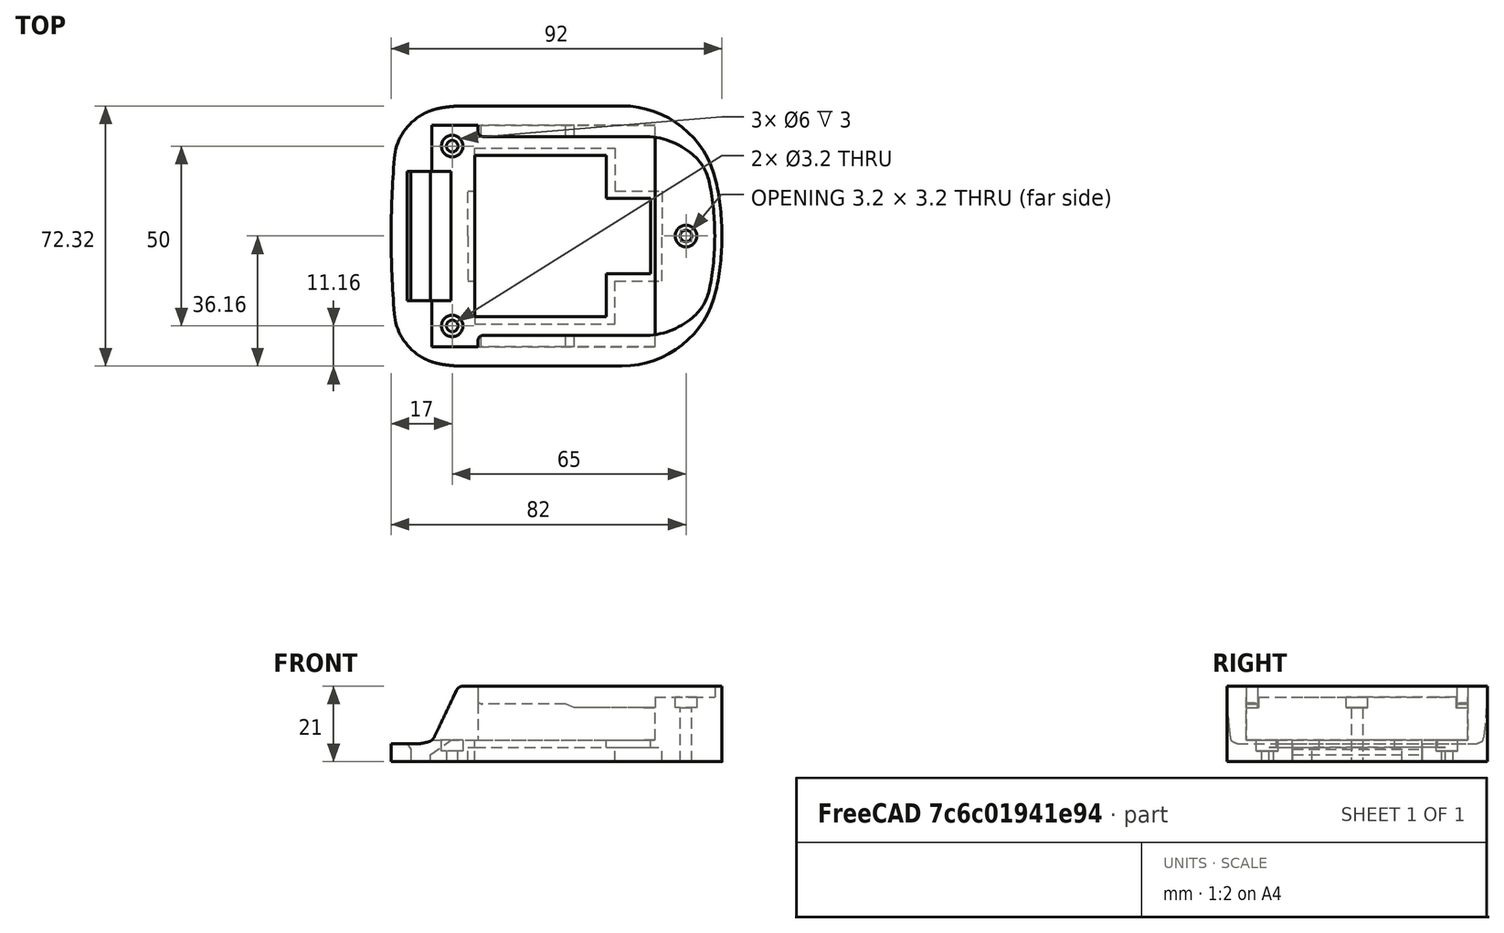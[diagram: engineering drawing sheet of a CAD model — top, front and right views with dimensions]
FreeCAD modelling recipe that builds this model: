
FCSTD DOCUMENT  (FreeCAD 0.21R33771 (Git))
Label: Makita LXT  - 18V - Battery holder
License: Creative Commons Attribution 4.0
LicenseURL: https://creativecommons.org/licenses/by/4.0/
objects: Sketcher::SketchObject×9, PartDesign::Pocket×8, Mesh::Feature×1, PartDesign::Pad×1, Part::Feature×1, PartDesign::Body×1
note: 29 computed .brp shape members not serialized (recipe doc carries the construction recipe); baked Part::Feature solids carry a one-line shape summary decoded from their .brp

FEATURE [Sketcher::SketchObject] Sketch
  FullyConstrained = false
  MapMode = 5
  Support = -> [XY_Plane]
  sketch-geometry (26):
    g0: ArcOfCircle CenterX=259.65 CenterY=-2.5774e-06 CenterZ=0 NormalX=0 NormalY=0 NormalZ=1 AngleXU=0 Radius=259.65 StartAngle=3.05831 EndAngle=3.14159
    g1: ArcOfCircle CenterX=16.3351 CenterY=20.3115 CenterZ=0 NormalX=0 NormalY=0 NormalZ=1 AngleXU=0 Radius=15.4888 StartAngle=1.76803 EndAngle=3.05831
    g2: LineSegment StartX=20 StartY=36.1629 StartZ=0 EndX=64.2 EndY=36.1629 EndZ=0
    g3: ArcOfCircle CenterX=64.2 CenterY=9.3939 CenterZ=0 NormalX=0 NormalY=0 NormalZ=1 AngleXU=0 Radius=26.769 StartAngle=0.218634 EndAngle=1.5708
    g4: ArcOfCircle CenterX=21.9206 CenterY=0 CenterZ=0 NormalX=0 NormalY=0 NormalZ=1 AngleXU=0 Radius=70.0794 StartAngle=0 EndAngle=0.218634
    g5: ArcOfCircle CenterX=20 CenterY=1.97116 CenterZ=0 NormalX=0 NormalY=0 NormalZ=1 AngleXU=0 Radius=34.1917 StartAngle=1.5708 EndAngle=1.76803
    g6: Circle CenterX=17 CenterY=25 CenterZ=0 NormalX=0 NormalY=0 NormalZ=1 AngleXU=0 Radius=1.6
    g7: ArcOfCircle CenterX=82 CenterY=0 CenterZ=0 NormalX=0 NormalY=0 NormalZ=1 AngleXU=0 Radius=1.6 StartAngle=0 EndAngle=3.14159
    g8: LineSegment StartX=23.3 StartY=0 StartZ=0 EndX=23.3 EndY=22.4 EndZ=0
    g9: LineSegment StartX=23.3 StartY=22.4 StartZ=0 EndX=59.9 EndY=22.4 EndZ=0
    g10: LineSegment StartX=59.9 StartY=22.4 StartZ=0 EndX=59.9 EndY=10.5 EndZ=0
    g11: LineSegment StartX=59.9 StartY=10.5 StartZ=0 EndX=72.1 EndY=10.5 EndZ=0
    g12: LineSegment StartX=72.1 StartY=10.5 StartZ=0 EndX=72.1 EndY=0 EndZ=0
    g13: ArcOfCircle CenterX=259.65 CenterY=2.5774e-06 CenterZ=0 NormalX=0 NormalY=0 NormalZ=1 AngleXU=0 Radius=259.65 StartAngle=3.14159 EndAngle=3.22488
    g14: ArcOfCircle CenterX=16.3351 CenterY=-20.3115 CenterZ=0 NormalX=0 NormalY=0 NormalZ=1 AngleXU=0 Radius=15.4888 StartAngle=3.22488 EndAngle=4.51516
    g15: LineSegment StartX=20 StartY=-36.1629 StartZ=0 EndX=64.2 EndY=-36.1629 EndZ=0
    g16: ArcOfCircle CenterX=64.2 CenterY=-9.3939 CenterZ=0 NormalX=0 NormalY=0 NormalZ=1 AngleXU=0 Radius=26.769 StartAngle=4.71239 EndAngle=6.06455
    g17: ArcOfCircle CenterX=21.9206 CenterY=0 CenterZ=0 NormalX=0 NormalY=0 NormalZ=1 AngleXU=0 Radius=70.0794 StartAngle=6.06455 EndAngle=6.28319
    g18: ArcOfCircle CenterX=20 CenterY=-1.97116 CenterZ=0 NormalX=0 NormalY=0 NormalZ=1 AngleXU=0 Radius=34.1917 StartAngle=4.51516 EndAngle=4.71239
    g19: Circle CenterX=17 CenterY=-25 CenterZ=0 NormalX=0 NormalY=0 NormalZ=1 AngleXU=0 Radius=1.6
    g20: ArcOfCircle CenterX=82 CenterY=0 CenterZ=0 NormalX=0 NormalY=0 NormalZ=1 AngleXU=0 Radius=1.6 StartAngle=3.14159 EndAngle=6.28319
    g21: LineSegment StartX=23.3 StartY=0 StartZ=0 EndX=23.3 EndY=-22.4 EndZ=0
    g22: LineSegment StartX=23.3 StartY=-22.4 StartZ=0 EndX=59.9 EndY=-22.4 EndZ=0
    g23: LineSegment StartX=59.9 StartY=-22.4 StartZ=0 EndX=59.9 EndY=-10.5 EndZ=0
    g24: LineSegment StartX=59.9 StartY=-10.5 StartZ=0 EndX=72.1 EndY=-10.5 EndZ=0
    g25: LineSegment StartX=72.1 StartY=-10.5 StartZ=0 EndX=72.1 EndY=0 EndZ=0
  constraints (59):
    c: Horizontal(g2)
    c: DistanceX(g2) = 20
    c: DistanceX(g2,g2) = 44.2
    c: Tangent(g4,g3) = -1.5708
    c: Tangent(g3,g2) = 1.5708
    c: Tangent(g1,g0) = -1.5708
    c: Tangent(g5,g2) = 1.5708
    c: Tangent(g5,g1) = -1.5708
    c: DistanceX(g0) = 0.9
    c: DistanceX(g1) = 13.3
    c: DistanceX(g4) = 92
    c: Coincident(g0,g-1)
    c: DistanceY(g0) = 21.6
    c: DistanceY(g1) = 35.5
    c: PointOnObject(g4,g-1)
    c: DistanceY(g3) = 15.2
    c: DistanceY(g6) = 25
    c: DistanceX(g6) = 17
    c: Diameter(g6) = 3.2
    c: PointOnObject(g7,g-1)
    c: PointOnObject(g7,g-1)
    c: PointOnObject(g7,g-1)
    c: DistanceX(g6,g7) = 65
    c: Equal(g7,g6)
    c: Tangent(g0,g-2)
    c: Perpendicular(g4,g-1)
    c: PointOnObject(g8,g-1)
    c: Vertical(g8)
    c: Coincident(g8,g9)
    c: Horizontal(g9)
    c: Coincident(g9,g10)
    c: Vertical(g10)
    c: Coincident(g10,g11)
    c: Horizontal(g11)
    c: Coincident(g11,g12)
    c: Vertical(g12)
    c: DistanceX(g8) = 23.3
    c: DistanceY(g8) = 22.4
    c: DistanceX(g9,g9) = 36.6
    c: DistanceY(g10,g10) = 11.9
    c: DistanceX(g11,g11) = 12.2
    c: PointOnObject(g12,g-1)
    c: Horizontal(g15)
    c: Tangent(g17,g16) = -1.5708
    c: Tangent(g16,g15) = -1.5708
    c: Tangent(g14,g13) = -1.5708
    c: Tangent(g18,g15) = -1.5708
    c: Tangent(g18,g14) = -1.5708
    c: Diameter(g19) = 3.2
    c: Equal(g20,g19)
    c: Vertical(g21)
    c: Coincident(g21,g22)
    c: Horizontal(g22)
    c: Coincident(g22,g23)
    c: Vertical(g23)
    c: Coincident(g23,g24)
    c: Horizontal(g24)
    c: Coincident(g24,g25)
    c: Vertical(g25)
FEATURE [Mesh::Feature] Makita_18V_Body  label="Makita 18V-Body"
  Placement = pos=(17,0,0) rot=(0,0,1;0rad)
FEATURE [PartDesign::Pad] Pad
  Direction = (0,0,1)
  Length = 21
  Length2 = 10
  Profile = -> Sketch
  ReferenceAxis = -> Sketch [N_Axis]
  Type = 0
FEATURE [Sketcher::SketchObject] Sketch001
  FullyConstrained = true
  MapMode = 5
  Placement = pos=(0,0,0) rot=(1,0,0;1.5708rad)
  Support = -> [XZ_Plane]
  sketch-geometry (8):
    g0: LineSegment StartX=0 StartY=5 StartZ=0 EndX=0 EndY=21 EndZ=0
    g1: LineSegment StartX=0 StartY=21 StartZ=0 EndX=20 EndY=21 EndZ=0
    g2: LineSegment StartX=0 StartY=5 StartZ=0 EndX=7.9 EndY=5 EndZ=0
    g3: LineSegment StartX=18.2 StartY=19.8659 StartZ=0 EndX=11.9 EndY=6.7 EndZ=0
    g4: ArcOfCircle CenterX=20 CenterY=19.0045 CenterZ=0 NormalX=0 NormalY=0 NormalZ=1 AngleXU=0 Radius=1.99546 StartAngle=1.5708 EndAngle=2.69528
    g5: ArcOfCircle CenterX=10.0257 CenterY=7.59685 CenterZ=0 NormalX=0 NormalY=0 NormalZ=1 AngleXU=0 Radius=2.07779 StartAngle=4.99242 EndAngle=5.83688
    g6: ArcOfCircle CenterX=7.9 CenterY=5.60003 CenterZ=0 NormalX=0 NormalY=0 NormalZ=1 AngleXU=0 Radius=0.600034 StartAngle=4.71239 EndAngle=4.87983
    g7: ArcOfCircle CenterX=4.0509 CenterY=28.3729 CenterZ=0 NormalX=0 NormalY=0 NormalZ=1 AngleXU=0 Radius=23.6959 StartAngle=4.87983 EndAngle=4.99242
  constraints (22):
    c: PointOnObject(g0,g-2)
    c: PointOnObject(g0,g-2)
    c: Horizontal(g1)
    c: Coincident(g1,g0)
    c: DistanceY(g0) = 5
    c: DistanceY(g0) = 21
    c: Coincident(g2,g0)
    c: Horizontal(g2)
    c: Tangent(g4,g3) = -1.5708
    c: Tangent(g5,g3) = 1.5708
    c: Tangent(g4,g1) = 1.5708
    c: DistanceX(g1,g1) = 20
    c: DistanceX(g3) = 11.9
    c: DistanceY(g3) = 6.7
    c: DistanceX(g3) = 18.2
    c: Tangent(g6,g2) = -1.5708
    c: DistanceX(g2,g2) = 7.9
    c: Tangent(g7,g5) = -1.5708
    c: Tangent(g7,g6) = -1.5708
    c: DistanceX(g2,g6) = 0.1
    c: DistanceX(g5) = 10.6
    c: DistanceY(g5) = 5.6
FEATURE [PartDesign::Pocket] Pocket
  BaseFeature = -> Pad
  Direction = (0,1,-2e-16)
  Length = 5
  Length2 = 5
  Midplane = true
  Profile = -> Sketch001
  ReferenceAxis = -> Sketch001 [N_Axis]
  Type = 1
FEATURE [Part::Feature] Makita_18V_Body001
  shape: bbox 92 x 71 x 21 mm, 5406 faces, 0 solids (baked)
FEATURE [Sketcher::SketchObject] Sketch002
  FullyConstrained = false
  MapMode = 5
  Placement = pos=(0,0,21) rot=(0,0,1;0rad)
  Support = -> [Pocket]
  sketch-geometry (16):
    g0: LineSegment StartX=24.2 StartY=30.78 StartZ=0 EndX=0 EndY=30.78 EndZ=0
    g1: LineSegment StartX=24.2 StartY=30.78 StartZ=0 EndX=24.2 EndY=28.88 EndZ=0
    g2: LineSegment StartX=25.4 StartY=27.68 StartZ=0 EndX=70.2 EndY=27.68 EndZ=0
    g3: ArcOfCircle CenterX=25.4 CenterY=28.88 CenterZ=0 NormalX=0 NormalY=0 NormalZ=1 AngleXU=0 Radius=1.2 StartAngle=3.14159 EndAngle=4.71239
    g4: ArcOfCircle CenterX=15.7361 CenterY=0 CenterZ=0 NormalX=0 NormalY=0 NormalZ=1 AngleXU=0 Radius=74.2639 StartAngle=0 EndAngle=0.199259
    g5: ArcOfCircle CenterX=74.666 CenterY=11.9002 CenterZ=0 NormalX=0 NormalY=0 NormalZ=1 AngleXU=0 Radius=14.1444 StartAngle=0.199259 EndAngle=0.868771
    g6: ArcOfCircle CenterX=70.2 CenterY=6.61972 CenterZ=0 NormalX=0 NormalY=0 NormalZ=1 AngleXU=0 Radius=21.0603 StartAngle=0.868771 EndAngle=1.5708
    g7: LineSegment StartX=0 StartY=0 StartZ=0 EndX=0 EndY=30.78 EndZ=0
    g8: LineSegment StartX=24.2 StartY=-30.78 StartZ=0 EndX=0 EndY=-30.78 EndZ=0
    g9: LineSegment StartX=24.2 StartY=-30.78 StartZ=0 EndX=24.2 EndY=-28.88 EndZ=0
    g10: LineSegment StartX=25.4 StartY=-27.68 StartZ=0 EndX=70.2 EndY=-27.68 EndZ=0
    g11: ArcOfCircle CenterX=25.4 CenterY=-28.88 CenterZ=0 NormalX=0 NormalY=0 NormalZ=1 AngleXU=0 Radius=1.2 StartAngle=1.5708 EndAngle=3.14159
    g12: ArcOfCircle CenterX=15.7361 CenterY=0 CenterZ=0 NormalX=0 NormalY=0 NormalZ=1 AngleXU=0 Radius=74.2639 StartAngle=6.08393 EndAngle=6.28319
    g13: ArcOfCircle CenterX=74.666 CenterY=-11.9002 CenterZ=0 NormalX=0 NormalY=0 NormalZ=1 AngleXU=0 Radius=14.1444 StartAngle=5.41441 EndAngle=6.08393
    g14: ArcOfCircle CenterX=70.2 CenterY=-6.61972 CenterZ=0 NormalX=0 NormalY=0 NormalZ=1 AngleXU=0 Radius=21.0603 StartAngle=4.71239 EndAngle=5.41441
    g15: LineSegment StartX=0 StartY=0 StartZ=0 EndX=0 EndY=-30.78 EndZ=0
  constraints (36):
    c: PointOnObject(g0,g-2)
    c: Horizontal(g0)
    c: DistanceY(g0) = 30.78
    c: DistanceX(g0,g0) = 24.2
    c: Coincident(g1,g0)
    c: Vertical(g1)
    c: Horizontal(g2)
    c: Tangent(g3,g1) = -1.5708
    c: Tangent(g3,g2) = -1.5708
    c: DistanceY(g1,g1) = 1.9
    c: Radius(g3) = 1.2
    c: PointOnObject(g4,g-1)
    c: Perpendicular(g4,g-1)
    c: DistanceX(g4) = 90
    c: DistanceY(g4) = 14.7
    c: Tangent(g6,g5) = -1.5708
    c: Tangent(g5,g4) = -1.5708
    c: Tangent(g6,g2) = 1.5708
    c: DistanceX(g2,g2) = 44.8
    c: DistanceX(g5) = 83.8
    c: DistanceY(g5) = 22.7
    c: PointOnObject(g7,g-1)
    c: Coincident(g7,g0)
    c: Vertical(g7)
    c: Horizontal(g8)
    c: Coincident(g9,g8)
    c: Vertical(g9)
    c: Horizontal(g10)
    c: Tangent(g11,g9) = 1.5708
    c: Tangent(g11,g10) = 1.5708
    c: Radius(g11) = 1.2
    c: Tangent(g14,g13) = -1.5708
    c: Tangent(g13,g12) = -1.5708
    c: Tangent(g14,g10) = -1.5708
    c: Coincident(g15,g8)
    c: Vertical(g15)
FEATURE [PartDesign::Pocket] Pocket001
  BaseFeature = -> Pocket
  Direction = (0,0,-1)
  Length = 3
  Length2 = 5
  Profile = -> Sketch002
  ReferenceAxis = -> Sketch002 [N_Axis]
  Type = 0
FEATURE [Sketcher::SketchObject] Sketch003
  ExternalGeometry = -> [Sketch002]
  FullyConstrained = false
  MapMode = 5
  Placement = pos=(0,0,18) rot=(0,0,1;0rad)
  Support = -> [Pocket001]
  sketch-geometry (14):
    g0: LineSegment StartX=0 StartY=0 StartZ=0 EndX=0 EndY=30.78 EndZ=0
    g1: LineSegment StartX=0 StartY=30.78 StartZ=0 EndX=24.2 EndY=30.78 EndZ=0
    g2: LineSegment StartX=24.2 StartY=28.88 StartZ=0 EndX=24.2 EndY=30.78 EndZ=0
    g3: LineSegment StartX=25.4 StartY=27.68 StartZ=0 EndX=70.2 EndY=27.68 EndZ=0
    g4: ArcOfCircle CenterX=25.4 CenterY=28.88 CenterZ=0 NormalX=0 NormalY=0 NormalZ=1 AngleXU=0 Radius=1.2 StartAngle=3.14159 EndAngle=4.71239
    g5: LineSegment StartX=73.4 StartY=27.4355 StartZ=0 EndX=73.4 EndY=0 EndZ=0
    g6: ArcOfCircle CenterX=70.2 CenterY=6.61972 CenterZ=0 NormalX=0 NormalY=0 NormalZ=1 AngleXU=0 Radius=21.0603 StartAngle=1.41826 EndAngle=1.5708
    g7: LineSegment StartX=0 StartY=0 StartZ=0 EndX=0 EndY=-30.78 EndZ=0
    g8: LineSegment StartX=0 StartY=-30.78 StartZ=0 EndX=24.2 EndY=-30.78 EndZ=0
    g9: LineSegment StartX=24.2 StartY=-28.88 StartZ=0 EndX=24.2 EndY=-30.78 EndZ=0
    g10: LineSegment StartX=25.4 StartY=-27.68 StartZ=0 EndX=70.2 EndY=-27.68 EndZ=0
    g11: ArcOfCircle CenterX=25.4 CenterY=-28.88 CenterZ=0 NormalX=0 NormalY=0 NormalZ=1 AngleXU=0 Radius=1.2 StartAngle=1.5708 EndAngle=3.14159
    g12: LineSegment StartX=73.4 StartY=-27.4355 StartZ=0 EndX=73.4 EndY=0 EndZ=0
    g13: ArcOfCircle CenterX=70.2 CenterY=-6.61972 CenterZ=0 NormalX=0 NormalY=0 NormalZ=1 AngleXU=0 Radius=21.0603 StartAngle=4.71239 EndAngle=4.86492
  constraints (23):
    c: Coincident(g0,g-3)
    c: Coincident(g0,g-4)
    c: Coincident(g1,g0)
    c: Coincident(g1,g-4)
    c: Coincident(g2,g-7)
    c: Coincident(g2,g1)
    c: Coincident(g3,g-5)
    c: Coincident(g3,g-6)
    c: Coincident(g4,g2)
    c: Tangent(g4,g3) = -1.5708
    c: PointOnObject(g5,g-6)
    c: PointOnObject(g5,g-1)
    c: Vertical(g5)
    c: Coincident(g6,g5)
    c: Tangent(g6,g3) = 1.5708
    c: DistanceX(g5) = 73.4
    c: Coincident(g8,g7)
    c: Coincident(g9,g8)
    c: Coincident(g11,g9)
    c: Tangent(g11,g10) = 1.5708
    c: Vertical(g12)
    c: Coincident(g13,g12)
    c: Tangent(g13,g10) = -1.5708
FEATURE [PartDesign::Pocket] Pocket002
  BaseFeature = -> Pocket001
  Direction = (0,0,-1)
  Length = 12
  Length2 = 5
  Profile = -> Sketch003
  ReferenceAxis = -> Sketch003 [N_Axis]
  Type = 0
FEATURE [Sketcher::SketchObject] Sketch004
  ExternalGeometry = -> [Pocket002]
  FullyConstrained = true
  MapMode = 5
  Placement = pos=(0,0,6) rot=(0,0,1;0rad)
  Support = -> [Pocket002]
  sketch-geometry (2):
    g0: Circle CenterX=17 CenterY=25 CenterZ=0 NormalX=0 NormalY=0 NormalZ=1 AngleXU=0 Radius=3
    g1: Circle CenterX=17 CenterY=-25 CenterZ=0 NormalX=0 NormalY=0 NormalZ=1 AngleXU=0 Radius=3
  constraints (4):
    c: Symmetric(g1,g0,g-1)
    c: Equal(g0,g1)
    c: Coincident(g-3,g0)
    c: Diameter(g0) = 6
FEATURE [PartDesign::Pocket] Pocket003
  BaseFeature = -> Pocket002
  Direction = (0,0,-1)
  Length = 3
  Length2 = 5
  Profile = -> Sketch004
  ReferenceAxis = -> Sketch004 [N_Axis]
  Type = 0
FEATURE [Sketcher::SketchObject] Sketch005
  ExternalGeometry = -> [Pocket003]
  FullyConstrained = true
  MapMode = 5
  Placement = pos=(0,0,18) rot=(0,0,1;0rad)
  Support = -> [Pocket003]
  sketch-geometry (1):
    g0: Circle CenterX=82 CenterY=0 CenterZ=0 NormalX=0 NormalY=0 NormalZ=1 AngleXU=0 Radius=3
  constraints (2):
    c: Coincident(g0,g-3)
    c: Diameter(g0) = 6
FEATURE [PartDesign::Pocket] Pocket004
  BaseFeature = -> Pocket003
  Direction = (0,0,-1)
  Length = 3
  Length2 = 5
  Profile = -> Sketch005
  ReferenceAxis = -> Sketch005 [N_Axis]
  Type = 0
FEATURE [Sketcher::SketchObject] Sketch006
  ExternalGeometry = -> [Sketch003]
  FullyConstrained = true
  MapMode = 5
  Placement = pos=(0,0,0) rot=(1,0,0;1.5708rad)
  Support = -> [XZ_Plane]
  sketch-geometry (7):
    g0: LineSegment StartX=73.4 StartY=15 StartZ=0 EndX=51 EndY=15 EndZ=0
    g1: LineSegment StartX=51 StartY=15 StartZ=0 EndX=48.5 EndY=16 EndZ=0
    g2: LineSegment StartX=48.5 StartY=16 StartZ=0 EndX=25 EndY=16 EndZ=0
    g3: LineSegment StartX=24.2 StartY=16.4 StartZ=0 EndX=25 EndY=16 EndZ=0
    g4: LineSegment StartX=24.2 StartY=16.4 StartZ=0 EndX=24.2 EndY=6 EndZ=0
    g5: LineSegment StartX=24.2 StartY=6 StartZ=0 EndX=73.4 EndY=6 EndZ=0
    g6: LineSegment StartX=73.4 StartY=6 StartZ=0 EndX=73.4 EndY=15 EndZ=0
  constraints (21):
    c: Horizontal(g0)
    c: Coincident(g1,g0)
    c: Coincident(g2,g1)
    c: Horizontal(g2)
    c: Coincident(g2,g3)
    c: Coincident(g4,g3)
    c: Vertical(g4)
    c: Coincident(g5,g4)
    c: Horizontal(g5)
    c: Coincident(g6,g5)
    c: Coincident(g6,g0)
    c: Vertical(g6)
    c: Vertical(g0,g-3)
    c: Vertical(g3,g-5)
    c: DistanceY(g4) = 6
    c: DistanceY(g4,g4) = 10.4
    c: DistanceY(g2) = 16
    c: DistanceX(g3,g2) = 0.8
    c: DistanceX(g2,g2) = 23.5
    c: DistanceY(g0) = 15
    c: DistanceX(g1,g0) = 2.5
FEATURE [PartDesign::Pocket] Pocket005
  BaseFeature = -> Pocket004
  Direction = (0,1,-2e-16)
  Length = 61.6
  Length2 = 5
  Midplane = true
  Profile = -> Sketch006
  ReferenceAxis = -> Sketch006 [N_Axis]
  Type = 0
FEATURE [Sketcher::SketchObject] Sketch007
  ExternalGeometry = -> [Pocket005]
  FullyConstrained = false
  MapMode = 5
  Placement = pos=(0,0,0) rot=(1,0,0;3.14159rad)
  Support = -> [Pocket005]
  sketch-geometry (14):
    g0: LineSegment StartX=21.3 StartY=0 StartZ=0 EndX=21.3 EndY=12.5 EndZ=0
    g1: LineSegment StartX=21.3 StartY=12.5 StartZ=0 EndX=23.3 EndY=12.5 EndZ=0
    g2: LineSegment StartX=23.3 StartY=12.5 StartZ=0 EndX=23.3 EndY=24.5 EndZ=0
    g3: LineSegment StartX=23.3 StartY=24.5 StartZ=0 EndX=62.3 EndY=24.5 EndZ=0
    g4: LineSegment StartX=62.3 StartY=24.5 StartZ=0 EndX=62.3 EndY=12.5 EndZ=0
    g5: LineSegment StartX=62.3 StartY=12.5 StartZ=0 EndX=75.3 EndY=12.5 EndZ=0
    g6: LineSegment StartX=75.3 StartY=12.5 StartZ=0 EndX=75.3 EndY=0 EndZ=0
    g7: LineSegment StartX=21.3 StartY=0 StartZ=0 EndX=21.3 EndY=-12.5 EndZ=0
    g8: LineSegment StartX=21.3 StartY=-12.5 StartZ=0 EndX=23.3 EndY=-12.5 EndZ=0
    g9: LineSegment StartX=23.3 StartY=-12.5 StartZ=0 EndX=23.3 EndY=-24.5 EndZ=0
    g10: LineSegment StartX=23.3 StartY=-24.5 StartZ=0 EndX=62.3 EndY=-24.5 EndZ=0
    g11: LineSegment StartX=62.3 StartY=-24.5 StartZ=0 EndX=62.3 EndY=-12.5 EndZ=0
    g12: LineSegment StartX=62.3 StartY=-12.5 StartZ=0 EndX=75.3 EndY=-12.5 EndZ=0
    g13: LineSegment StartX=75.3 StartY=-12.5 StartZ=0 EndX=75.3 EndY=0 EndZ=0
  constraints (35):
    c: PointOnObject(g0,g-1)
    c: Vertical(g0)
    c: Coincident(g0,g1)
    c: PointOnObject(g1,g-3)
    c: Horizontal(g1)
    c: Coincident(g1,g2)
    c: Vertical(g2)
    c: Coincident(g2,g3)
    c: Horizontal(g3)
    c: Coincident(g3,g4)
    c: Vertical(g4)
    c: Coincident(g4,g5)
    c: Horizontal(g5)
    c: Coincident(g5,g6)
    c: PointOnObject(g6,g-1)
    c: Vertical(g6)
    c: DistanceY(g2) = 24.5
    c: DistanceY(g0,g0) = 12.5
    c: DistanceX(g1,g1) = 2
    c: DistanceX(g-4,g3) = 2.4
    c: DistanceY(g-5,g4) = 2
    c: DistanceX(g-5,g5) = 3.2
    c: Vertical(g7)
    c: Coincident(g7,g8)
    c: Horizontal(g8)
    c: Coincident(g8,g9)
    c: Vertical(g9)
    c: Coincident(g9,g10)
    c: Horizontal(g10)
    c: Coincident(g10,g11)
    c: Vertical(g11)
    c: Coincident(g11,g12)
    c: Horizontal(g12)
    c: Coincident(g12,g13)
    c: Vertical(g13)
FEATURE [PartDesign::Pocket] Pocket006
  BaseFeature = -> Pocket005
  Direction = (0,0,1)
  Length = 4
  Length2 = 5
  Profile = -> Sketch007
  ReferenceAxis = -> Sketch007 [N_Axis]
  Type = 0
FEATURE [Sketcher::SketchObject] Sketch008
  FullyConstrained = true
  MapMode = 5
  Placement = pos=(0,0,0) rot=(1,0,0;1.5708rad)
  Support = -> [XZ_Plane]
  sketch-geometry (7):
    g0: LineSegment StartX=5.5 StartY=0 StartZ=0 EndX=11 EndY=0 EndZ=0
    g1: LineSegment StartX=11 StartY=0 StartZ=0 EndX=11 EndY=2 EndZ=0
    g2: LineSegment StartX=11 StartY=2 StartZ=0 EndX=16.7 EndY=6 EndZ=0
    g3: LineSegment StartX=16.7 StartY=6 StartZ=0 EndX=4.45 EndY=6 EndZ=0
    g4: LineSegment StartX=4.45 StartY=6 StartZ=0 EndX=4.45 EndY=5 EndZ=0
    g5: LineSegment StartX=4.45 StartY=5 StartZ=0 EndX=5.5 EndY=3.5 EndZ=0
    g6: LineSegment StartX=5.5 StartY=3.5 StartZ=0 EndX=5.5 EndY=0 EndZ=0
  constraints (21):
    c: PointOnObject(g0,g-1)
    c: PointOnObject(g0,g-1)
    c: Coincident(g0,g1)
    c: Vertical(g1)
    c: Coincident(g1,g2)
    c: Coincident(g2,g3)
    c: Horizontal(g3)
    c: Coincident(g3,g4)
    c: Vertical(g4)
    c: Coincident(g4,g5)
    c: Coincident(g5,g6)
    c: Coincident(g6,g0)
    c: Vertical(g6)
    c: DistanceX(g0) = 5.5
    c: DistanceX(g0) = 11
    c: DistanceY(g6,g6) = 3.5
    c: DistanceY(g1,g1) = 2
    c: DistanceY(g2) = 6
    c: DistanceX(g2) = 16.7
    c: DistanceY(g4) = 5
    c: DistanceX(g4) = 4.45
FEATURE [PartDesign::Pocket] Pocket007
  BaseFeature = -> Pocket006
  Direction = (0,1,2e-16)
  Length = 36
  Length2 = 5
  Midplane = true
  Profile = -> Sketch008
  ReferenceAxis = -> Sketch008 [N_Axis]
  Type = 0
FEATURE [PartDesign::Body] Body  label="Battery mount"
  Group = -> [Sketch,Pad,Sketch001,Pocket,Sketch002,Pocket001,Sketch003,Pocket002,Sketch004,Pocket003,Sketch005,Pocket004,Sketch006,Pocket005,Sketch007,Pocket006,Sketch008,Pocket007]
  Origin = -> Origin
  Tip = -> Pocket007
